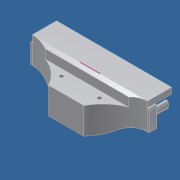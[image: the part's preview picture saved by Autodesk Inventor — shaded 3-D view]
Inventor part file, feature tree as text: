
AUTODESK INVENTOR PART (.ipt)
format: ipt  version: unknown  size: 439,296 bytes
history: native  units: in
note: dims shown in document units (in); Inventor stores cm internally (conversion verified against a paired STEP export)
features: other x21, sketch x11, extrude x8, chamfer x3, fillet x2, pattern_linear x2
ambient origin geometry x8: Origin, YZ Plane, XZ Plane, XY Plane, X Axis, Y Axis, Z Axis, Center Point
bodies: Solid2 (feature_tree), Solid3 (feature_tree)
feature tree (47):
  sketch  "Sketch1"  dims[d15=0.1437in d18=0.69in d19=-0.0069in]
  extrude  "Extrusion2"  Depth=0.69in
  extrude  "Extrusion3"  Depth=0.25in
  extrude  "Extrusion4"  Depth=0.06in
  sketch  "Sketch4"  dims[d36=2.0in d37=2.0in d39=0.7874in d41=2.0in d42=0.7874in d44=2.0in]
  fillet  "Fillet1"  Radius=0.076in
  extrude  "Extrusion5"  Depth=2.0in
  sketch  "Sketch7"  dims[d103=1.623in d104=0.0in d106=0.5in d107=0.0in]
  sketch  "Sketch8"  dims[d108=0.125in d109=0.125in d110=45.0deg d111=0.5in d112=0.125in d113=45.0deg d114=0.125in d115=0.125in d116=45.0deg]
  pattern_linear  "Rectangular Pattern1"  Count1=2 Spacing1=2.0in
  pattern_linear  "Rectangular Pattern2"  Count1=2 Spacing1=2.0in
  extrude  "Extrusion16"  Depth=0.75in
  extrude  "Extrusion18"  Depth=0.5in TaperAngle=0.0deg
  extrude  "Extrusion19"  Depth=0.5in TaperAngle=45.0deg
  chamfer  "Chamfer1"  Distance=0.125in Angle=45.0deg
  chamfer  "Chamfer2"  Distance=5.0in
  chamfer  "Chamfer3"  [1 undecoded]
  fillet  "Fillet10"  [1 undecoded]
  extrude  "Extrusion20"  [1 undecoded]
  sketch  "Sketch2"  dims[d25=0.25in d26=0.0in d27=0.25in]
  sketch  "Sketch3"  dims[d28=0.94in d29=0.0in d30=0.06in d31=0.076in d32=0.0in]
  sketch  "Sketch5"  dims[d95=4.85in d96=0.0in d102=0.75in]
  other  "Pattern of Solid2:1"
  sketch  "Sketch25"  dims[d117=0.125in]
  sketch  "Sketch26"  dims[d121=0.16in]
  sketch  "Sketch28"  dims[d122=0.16in d123=5.0in d124=0.0in]
  sketch  "Sketch29"
  other  "Composite1"
  other  "Composite2"
  other  "Composite3"
  other  "Composite4"
  other  "Composite5"
  other  "Composite6"
  other  "Composite7"
  other  "Composite8"
  other  "Composite9"
  other  "Composite10"
  other  "Srf1"
  other  "Srf2"
  other  "Srf3"
  other  "Srf4"
  other  "Srf5"
  other  "Srf6"
  other  "Srf7"
  other  "Srf8"
  other  "Srf9"
  other  "Srf10"
note: 3 required parameter values undecoded (feature->parameter linkage not recoverable at this tier; creation-order binding heuristic only, values carry confidence <= 0.55)
